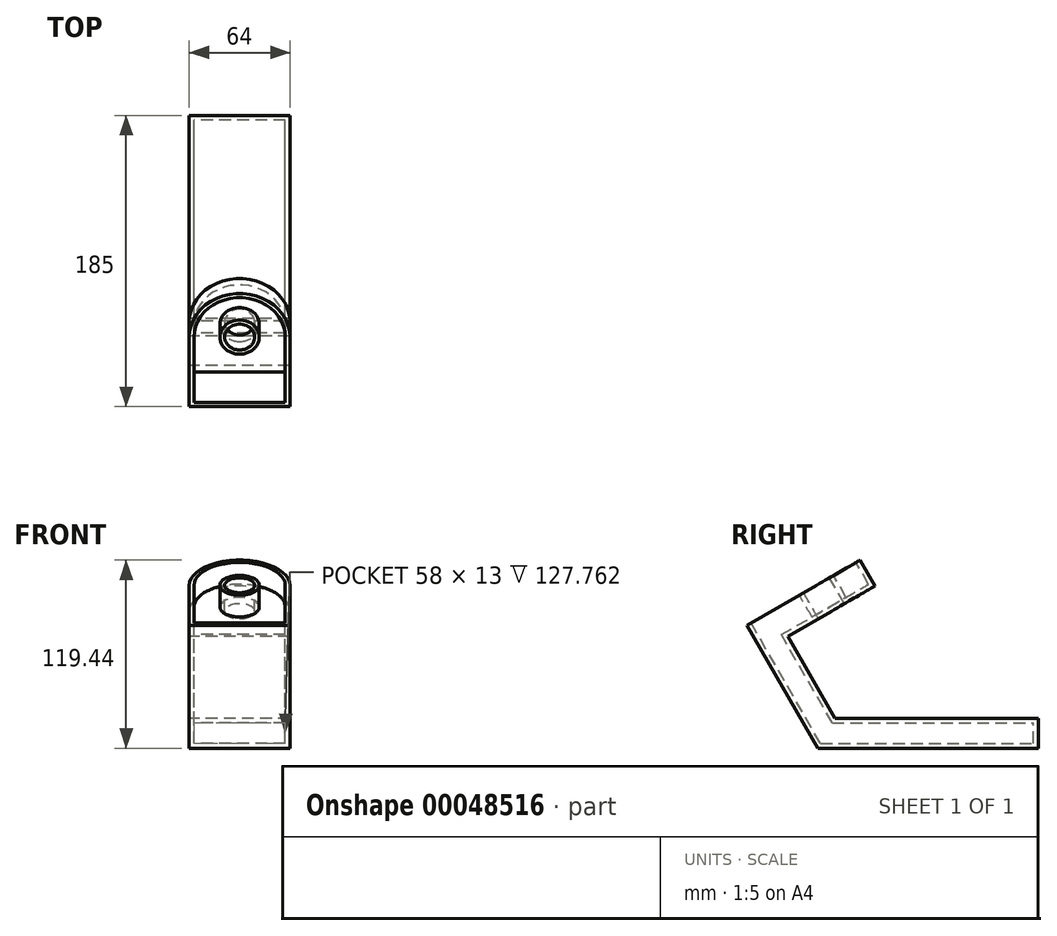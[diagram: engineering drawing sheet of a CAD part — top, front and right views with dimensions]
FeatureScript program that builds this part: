
annotation { "Feature Type Name" : "Feature", "Feature Type Description" : "" }
export const myFeature = defineFeature(function(context is Context, id is Id, definition is map)
    precondition{}
    {
        {
            var Q0;
            Q0=qCreatedBy(makeId("Right.planeOp"),FACE);
            var sketch = newSketch(context, id + "F0", { "sketchPlane" : qUnion([Q0])});
            skLineSegment(sketch, "E0", {"start": v(0, 0) * mm, "end": v(140, 0) * mm});
            skLineSegment(sketch, "E1", {"start": v(0, 0) * mm, "end": v(-45, 77.94) * mm});
            skLineSegment(sketch, "E2", {"start": v(-45, 77.94) * mm, "end": v(26.88, 119.44) * mm});
            skLineSegment(sketch, "E3.0", {"start": v(10.97, 19) * mm, "end": v(140, 19) * mm});
            skLineSegment(sketch, "E3.1", {"start": v(10.97, 19) * mm, "end": v(-19.05, 70.99) * mm});
            skLineSegment(sketch, "E3.2", {"start": v(-19.05, 70.99) * mm, "end": v(36.38, 102.99) * mm});
            skLineSegment(sketch, "E4", {"start": v(26.88, 119.44) * mm, "end": v(36.38, 102.99) * mm});
            skLineSegment(sketch, "E5", {"start": v(140, 0) * mm, "end": v(140, 19) * mm});
            skSolve(sketch);
        }
        {
            var Q0;
            Q0=makeQuery(id+"F0.imprint","IMPRINT",FACE,{"disambiguationData":[TD([[makeQuery(id+"F0.imprint","IMPRINT",EDGE,{"derivedFrom":sQuery(id+"F0.wireOp",EDGE,"E0")}),1.0]])]});
            extrude(context, id + "F1", {"entities" : qUnion([Q0]), "endBound" : BoundingType.SYMMETRIC, "depth" : 64 * mm});
        }
        {
            var Q0;
            Q0=makeQuery(id+"F1.opExtrude","CAP_EDGE",EDGE,{"disambiguationData":[OSD([sQuery(id+"F0.wireOp",EDGE,"E4")])],"isStart":false});
            var Q1;
            Q1=makeQuery(id+"F1.opExtrude","CAP_EDGE",EDGE,{"disambiguationData":[OSD([sQuery(id+"F0.wireOp",EDGE,"E4")])],"isStart":true});
            fillet(context, id + "F2", {"entities" : qUnion([Q0, Q1]), "radius" : 32 * mm, "tangentPropagation" : true, "rho" : 0, "crossSection" : FilletCrossSection.CONIC, "allowEdgeOverflow" : false});
        }
        {
            var Q0;
            Q0=makeQuery(id+"F1.opExtrude","SWEPT_FACE",FACE,{"disambiguationData":[OSD([sQuery(id+"F0.wireOp",EDGE,"E2")])]});
            var sketch = newSketch(context, id + "F3", { "sketchPlane" : qUnion([Q0])});
            skCircle(sketch, "E6", {"center": v(0, 51) * mm, "radius": 9.5 * mm});
            skLineSegment(sketch, "E7", {"start": v(-32, 51) * mm, "end": v(32, 51) * mm, "construction": true});
            skSolve(sketch);
        }
        {
            var Q0;
            Q0=makeQuery(id+"F3.imprint","IMPRINT",FACE,{"disambiguationData":[TD([[makeQuery(id+"F3.imprint","IMPRINT",EDGE,{"derivedFrom":sQuery(id+"F3.wireOp",EDGE,"E6")}),1.0]])]});
            extrude(context, id + "F4", {"entities" : qUnion([Q0]), "operationType" : NewBodyOperationType.REMOVE, "oppositeDirection" : true, "depth" : 25 * mm});
        }
        {
            var Q0;
            Q0=makeQuery(id+"F1.opExtrude","SWEPT_FACE",FACE,{"disambiguationData":[OSD([sQuery(id+"F0.wireOp",EDGE,"E2")])]});
            shell(context, id + "F5", {"entities" : qUnion([Q0]), "thickness" : 3 * mm});
        }
    });
